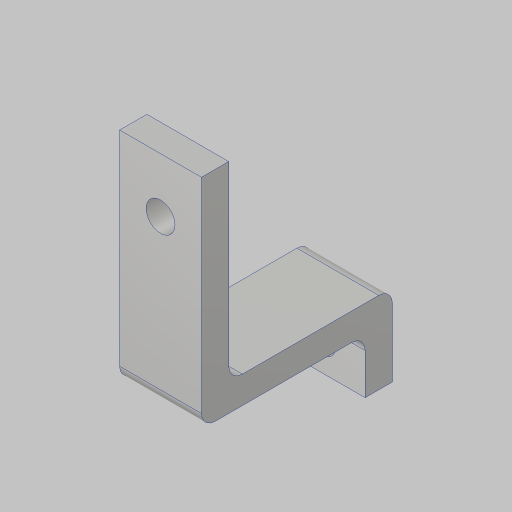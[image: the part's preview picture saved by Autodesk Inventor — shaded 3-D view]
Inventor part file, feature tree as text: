
AUTODESK INVENTOR PART (.ipt)
format: ipt  version: 2023.5 (Build 275446000, 446)  size: 122,880 bytes
history: native  units: in
note: dims shown in document units (in); Inventor stores cm internally (conversion verified against a paired STEP export)
features: sketch x3, hole x2, extrude x1, fillet x1
ambient origin geometry x8: Origin, YZ Plane, XZ Plane, XY Plane, X Axis, Y Axis, Z Axis, Center Point
bodies: Solid1 (feature_tree)
feature tree (7):
  extrude  "Extrusion1"  Depth=1.5in
  hole  "Hole1"  [1 undecoded]
  hole  "Hole2"  [1 undecoded]
  fillet  "Fillet1"  Radius=0.5in
  sketch  "Sketch1"  dims[d0=2.0in d1=1.5in]
  sketch  "Sketch2"  dims[d2=0.5in d3=0.25in]
  sketch  "Sketch3"  dims[d4=0.75in d5=0.0in d6=0.266in d7=0.75in d8=0.507in d9=0.25in d10=0.5635in d11=1.0in d12=0.8108in d13=0.201in d14=0.75in d15=0.385in d16=0.25in d17=0.5635in d18=1.0in d19=0.8108in d20=0.125in d21=0.5in]
note: 2 required parameter values undecoded (feature->parameter linkage not recoverable at this tier; creation-order binding heuristic only, values carry confidence <= 0.55)
